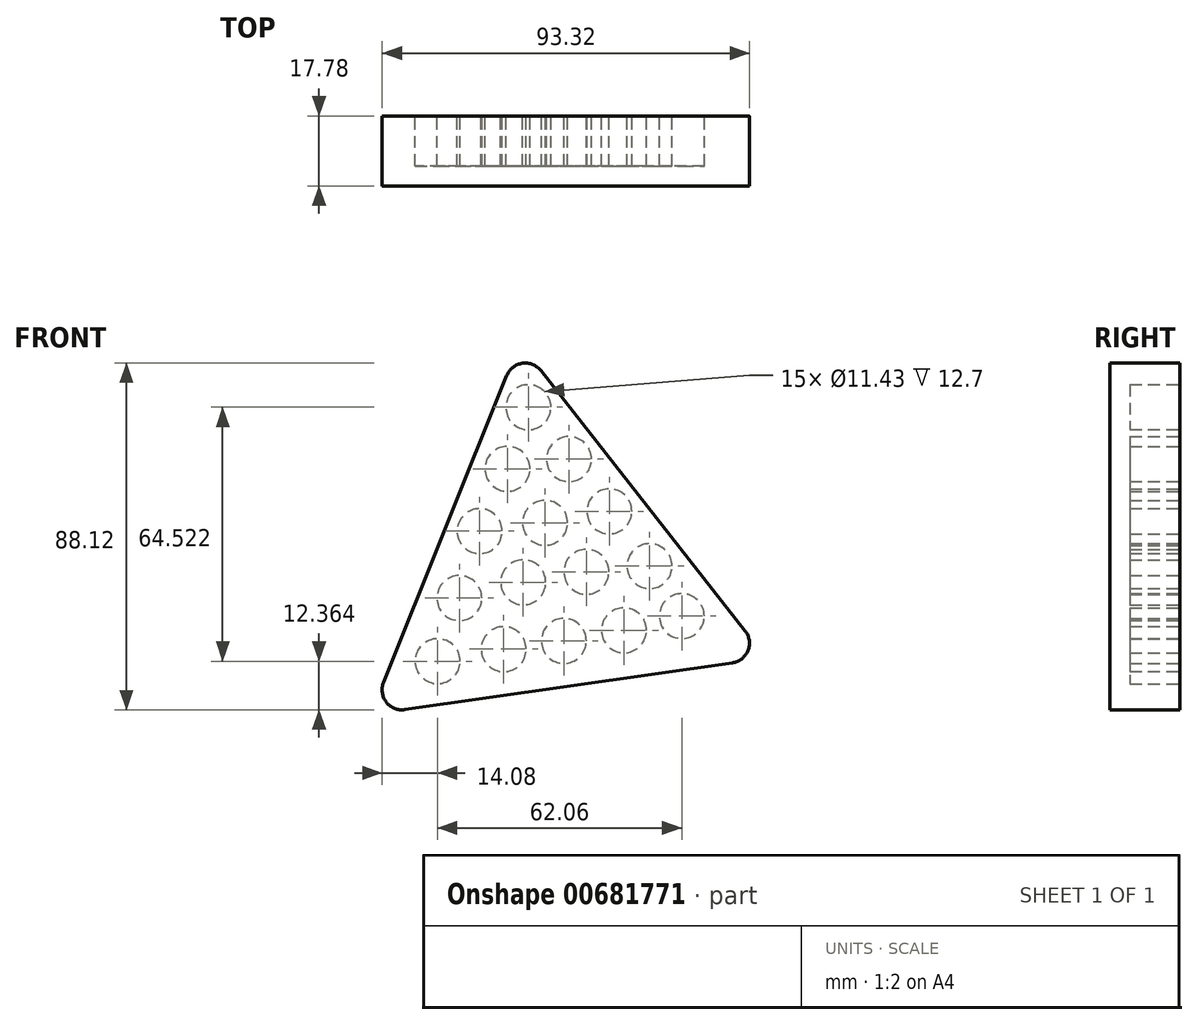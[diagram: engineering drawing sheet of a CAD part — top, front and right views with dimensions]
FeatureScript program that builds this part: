
annotation { "Feature Type Name" : "Feature", "Feature Type Description" : "" }
export const myFeature = defineFeature(function(context is Context, id is Id, definition is map)
    precondition{}
    {
        {
            var Q0;
            Q0=qCreatedBy(makeId("Front.planeOp"),FACE);
            var sketch = newSketch(context, id + "F0", { "sketchPlane" : qUnion([Q0])});
            skLineSegment(sketch, "E0", {"start": v(-41.91, -37.71) * mm, "end": v(-4.07, 56.57) * mm});
            skLineSegment(sketch, "E1", {"start": v(-4.07, 56.57) * mm, "end": v(58.66, -23.35) * mm});
            skLineSegment(sketch, "E2", {"start": v(58.66, -23.35) * mm, "end": v(-41.91, -37.71) * mm});
            skSolve(sketch);
        }
        {
            var Q0;
            Q0 = qSketchRegion(id + "F0", true);
            extrude(context, id + "F1", {"entities" : qUnion([Q0]), "depth" : 17.78 * mm, "offsetDistance" : 25.4 * mm});
        }
        {
            var Q0;
            Q0=makeQuery(id+"F1.opExtrude","SWEPT_EDGE",EDGE,{"disambiguationData":[OSD([sQuery(id+"F0.wireOp",EDGE,"E0"),sQuery(id+"F0.wireOp",EDGE,"E1")])]});
            var Q1;
            Q1=makeQuery(id+"F1.opExtrude","SWEPT_EDGE",EDGE,{"disambiguationData":[OSD([sQuery(id+"F0.wireOp",EDGE,"E1"),sQuery(id+"F0.wireOp",EDGE,"E2")])]});
            var Q2;
            Q2=makeQuery(id+"F1.opExtrude","SWEPT_EDGE",EDGE,{"disambiguationData":[OSD([sQuery(id+"F0.wireOp",EDGE,"E0"),sQuery(id+"F0.wireOp",EDGE,"E2")])]});
            fillet(context, id + "F2", {"entities" : qUnion([Q0, Q1, Q2]), "radius" : 5.08 * mm, "tangentPropagation" : true, "allowEdgeOverflow" : false});
        }
        {
            var Q0;
            Q0=makeQuery(id+"F1.opExtrude","CAP_FACE",FACE,{"disambiguationData":[OSD([sQuery(id+"F0.wireOp",EDGE,"E0"),sQuery(id+"F0.wireOp",EDGE,"E1"),sQuery(id+"F0.wireOp",EDGE,"E2")])],"isStart":true});
            var sketch = newSketch(context, id + "F3", { "sketchPlane" : qUnion([Q0])});
            skSolve(sketch);
        }
        {
            var Q0;
            {var subQ0=sQuery(id+"F0.wireOp",EDGE,"E0");Q0=makeQuery(id+"F3.imprint","IMPRINT",FACE,{"disambiguationData":[TD([[makeQuery(id+"F3.imprint","IMPRINT",EDGE,{"derivedFrom":makeQuery(id+"F1.opExtrude","CAP_EDGE",EDGE,{"disambiguationData":[OSD([subQ0])],"isStart":true})}),1.0]])]});}
            var sketch = newSketch(context, id + "F4", { "sketchPlane" : qUnion([Q0])});
            skCircle(sketch, "E3", {"center": v(1.84, 40.37) * mm, "radius": 5.72 * mm});
            skCircle(sketch, "E4", {"center": v(-8.47, 27.2) * mm, "radius": 5.72 * mm});
            skCircle(sketch, "E5", {"center": v(7.16, 24.73) * mm, "radius": 5.72 * mm});
            skCircle(sketch, "E6", {"center": v(-18.71, 13.92) * mm, "radius": 5.72 * mm});
            skCircle(sketch, "E7", {"center": v(-2.39, 10.98) * mm, "radius": 5.72 * mm});
            skCircle(sketch, "E8", {"center": v(14.23, 8.88) * mm, "radius": 5.72 * mm});
            skCircle(sketch, "E9", {"center": v(-12.89, -1.43) * mm, "radius": 5.72 * mm});
            skCircle(sketch, "E10", {"center": v(3.15, -4.1) * mm, "radius": 5.72 * mm});
            skCircle(sketch, "E11", {"center": v(19.38, -8.12) * mm, "radius": 5.72 * mm});
            skCircle(sketch, "E12", {"center": v(-22.44, -16.33) * mm, "radius": 5.72 * mm});
            skCircle(sketch, "E13", {"center": v(-7.16, -19) * mm, "radius": 5.72 * mm});
            skCircle(sketch, "E14", {"center": v(8.12, -21.1) * mm, "radius": 5.72 * mm});
            skPoint(sketch, "E15.center.orphan", {"position": v(-28.93, 0) * mm});
            skCircle(sketch, "E16", {"center": v(-28.93, 0) * mm, "radius": 5.72 * mm});
            skCircle(sketch, "E17", {"center": v(-37.14, -12.7) * mm, "radius": 5.72 * mm});
            skCircle(sketch, "E18", {"center": v(24.92, -24.16) * mm, "radius": 5.72 * mm});
            skSolve(sketch);
        }
        {
            var Q0;
            Q0 = qSketchRegion(id + "F4", true);
            extrude(context, id + "F5", {"entities" : qUnion([Q0]), "operationType" : NewBodyOperationType.REMOVE, "oppositeDirection" : true, "depth" : 12.7 * mm, "offsetDistance" : 25.4 * mm});
        }
    });
